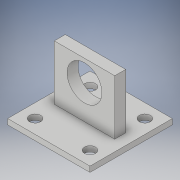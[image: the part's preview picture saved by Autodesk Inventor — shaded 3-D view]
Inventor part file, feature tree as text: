
AUTODESK INVENTOR PART (.ipt)
format: ipt  version: 2018 (Build 220112000, 112)  size: 143,872 bytes
history: native  units: in
note: dims shown in document units (in); Inventor stores cm internally (conversion verified against a paired STEP export)
features: extrude x4, sketch x4
ambient origin geometry x8: Origin, YZ Plane, XZ Plane, XY Plane, X Axis, Y Axis, Z Axis, Center Point
bodies: Solid1 (feature_tree)
feature tree (8):
  extrude  "Extrusion1"  Depth=1.5in
  extrude  "Extrusion2"  Depth=0.2in
  extrude  "Extrusion3"  Depth=0.65in
  extrude  "Extrusion4"  Depth=1.0in TaperAngle=0.0deg
  sketch  "Sketch1"  dims[d0=1.5in d1=1.5in]
  sketch  "Sketch2"  dims[d2=0.1in d3=0.0in d4=0.2in]
  sketch  "Sketch3"  dims[d5=0.2in d6=0.65in]
  sketch  "Sketch4"  dims[d7=0.2in d8=1.0in d9=0.0in d10=0.635in d11=2.0in d12=0.0in d13=0.2031in d14=0.2031in d15=0.2031in d16=0.2031in d17=0.25in d18=0.25in d19=0.25in d20=0.25in d21=0.25in d22=0.25in d23=0.25in d24=0.25in d25=2.0in d26=0.0in]
